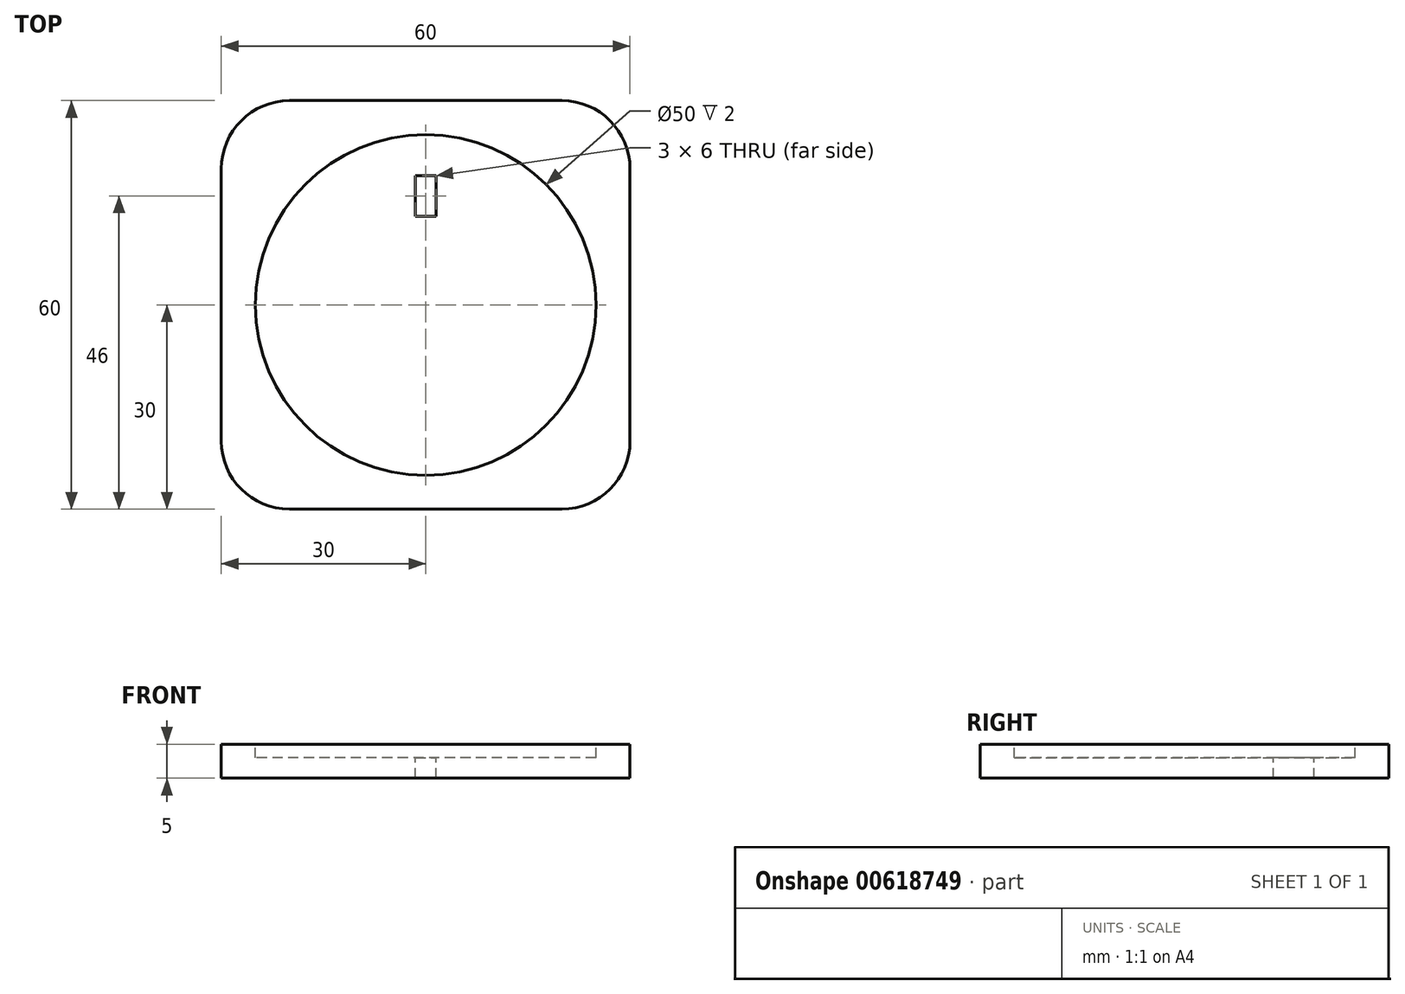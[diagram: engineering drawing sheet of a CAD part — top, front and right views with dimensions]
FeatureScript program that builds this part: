
annotation { "Feature Type Name" : "Feature", "Feature Type Description" : "" }
export const myFeature = defineFeature(function(context is Context, id is Id, definition is map)
    precondition{}
    {
        {
            var Q0;
            Q0=qCreatedBy(makeId("Top.planeOp"),FACE);
            var sketch = newSketch(context, id + "F0", { "sketchPlane" : qUnion([Q0])});
            skLineSegment(sketch, "E0.bottom", {"start": v(-30, 30) * mm, "end": v(30, 30) * mm});
            skLineSegment(sketch, "E0.top", {"start": v(-30, -30) * mm, "end": v(30, -30) * mm});
            skLineSegment(sketch, "E0.left", {"start": v(-30, 30) * mm, "end": v(-30, -30) * mm});
            skLineSegment(sketch, "E0.right", {"start": v(30, 30) * mm, "end": v(30, -30) * mm});
            skSolve(sketch);
        }
        {
            var Q0;
            Q0 = qSketchRegion(id + "F0", true);
            extrude(context, id + "F1", {"entities" : qUnion([Q0]), "depth" : 5 * mm, "offsetDistance" : 25 * mm});
        }
        {
            var Q0;
            Q0=makeQuery(id+"F1.opExtrude","SWEPT_EDGE",EDGE,{"disambiguationData":[OSD([sQuery(id+"F0.wireOp",EDGE,"E0.bottom"),sQuery(id+"F0.wireOp",EDGE,"E0.left")])]});
            var Q1;
            Q1=makeQuery(id+"F1.opExtrude","SWEPT_EDGE",EDGE,{"disambiguationData":[OSD([sQuery(id+"F0.wireOp",EDGE,"E0.top"),sQuery(id+"F0.wireOp",EDGE,"E0.left")])]});
            var Q2;
            Q2=makeQuery(id+"F1.opExtrude","SWEPT_EDGE",EDGE,{"disambiguationData":[OSD([sQuery(id+"F0.wireOp",EDGE,"E0.bottom"),sQuery(id+"F0.wireOp",EDGE,"E0.right")])]});
            var Q3;
            Q3=makeQuery(id+"F1.opExtrude","SWEPT_EDGE",EDGE,{"disambiguationData":[OSD([sQuery(id+"F0.wireOp",EDGE,"E0.top"),sQuery(id+"F0.wireOp",EDGE,"E0.right")])]});
            fillet(context, id + "F2", {"entities" : qUnion([Q0, Q1, Q2, Q3]), "radius" : 10 * mm, "tangentPropagation" : true, "allowEdgeOverflow" : false});
        }
        {
            var Q0;
            Q0=makeQuery(id+"F1.opExtrude","CAP_FACE",FACE,{"disambiguationData":[OSD([sQuery(id+"F0.wireOp",EDGE,"E0.bottom"),sQuery(id+"F0.wireOp",EDGE,"E0.top"),sQuery(id+"F0.wireOp",EDGE,"E0.left"),sQuery(id+"F0.wireOp",EDGE,"E0.right")])],"isStart":false});
            var sketch = newSketch(context, id + "F3", { "sketchPlane" : qUnion([Q0])});
            skCircle(sketch, "E1", {"center": v(0, 0) * mm, "radius": 25 * mm});
            skSolve(sketch);
        }
        {
            var Q0;
            Q0=makeQuery(id+"F3.imprint","IMPRINT",FACE,{"disambiguationData":[TD([[makeQuery(id+"F3.imprint","IMPRINT",EDGE,{"derivedFrom":sQuery(id+"F3.wireOp",EDGE,"E1")}),1.0]])]});
            extrude(context, id + "F4", {"entities" : qUnion([Q0]), "operationType" : NewBodyOperationType.REMOVE, "oppositeDirection" : true, "depth" : 2 * mm, "offsetDistance" : 25 * mm});
        }
        {
            var Q0;
            Q0=makeQuery(id+"F4.boolean.opBoolean","COPY",FACE,{"derivedFrom":makeQuery(id+"F4.opExtrude","CAP_FACE",FACE,{"disambiguationData":[OSD([sQuery(id+"F3.wireOp",EDGE,"E1")])],"isStart":false})});
            var sketch = newSketch(context, id + "F5", { "sketchPlane" : qUnion([Q0])});
            skLineSegment(sketch, "E2.bottom", {"start": v(-1.5, 19) * mm, "end": v(1.5, 19) * mm});
            skLineSegment(sketch, "E2.top", {"start": v(-1.5, 13) * mm, "end": v(1.5, 13) * mm});
            skLineSegment(sketch, "E2.left", {"start": v(-1.5, 19) * mm, "end": v(-1.5, 13) * mm});
            skLineSegment(sketch, "E2.right", {"start": v(1.5, 19) * mm, "end": v(1.5, 13) * mm});
            skSolve(sketch);
        }
        {
            var Q0;
            Q0=makeQuery(id+"FNsAaD1DEC10Ost_1.3.F5.imprint","IMPRINT",FACE,{"disambiguationData":[TD([[makeQuery(id+"FNsAaD1DEC10Ost_1.3.F5.imprint","IMPRINT",EDGE,{"derivedFrom":sQuery(id+"FNsAaD1DEC10Ost_1.3.F5.wireOp",EDGE,"E2.bottom")}),-1.0]])]});
            var Q1;
            Q1=makeQuery(id+"FNsAaD1DEC10Ost_1.2.F5.imprint","IMPRINT",FACE,{"disambiguationData":[TD([[makeQuery(id+"FNsAaD1DEC10Ost_1.2.F5.imprint","IMPRINT",EDGE,{"derivedFrom":sQuery(id+"FNsAaD1DEC10Ost_1.2.F5.wireOp",EDGE,"E2.bottom")}),-1.0]])]});
            var Q2;
            Q2=makeQuery(id+"FNsAaD1DEC10Ost_1.1.F5.imprint","IMPRINT",FACE,{"disambiguationData":[TD([[makeQuery(id+"FNsAaD1DEC10Ost_1.1.F5.imprint","IMPRINT",EDGE,{"derivedFrom":sQuery(id+"FNsAaD1DEC10Ost_1.1.F5.wireOp",EDGE,"E2.bottom")}),-1.0]])]});
            var Q3;
            Q3=makeQuery(id+"F5.imprint","IMPRINT",FACE,{"disambiguationData":[TD([[makeQuery(id+"F5.imprint","IMPRINT",EDGE,{"derivedFrom":sQuery(id+"F5.wireOp",EDGE,"E2.bottom")}),-1.0]])]});
            extrude(context, id + "F6", {"entities" : qUnion([Q0, Q1, Q2, Q3]), "operationType" : NewBodyOperationType.REMOVE, "oppositeDirection" : true, "depth" : 3 * mm, "offsetDistance" : 25 * mm});
        }
    });
